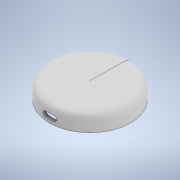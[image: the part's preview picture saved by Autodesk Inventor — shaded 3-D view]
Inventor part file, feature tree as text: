
AUTODESK INVENTOR PART (.ipt)
format: ipt  version: 2021 (Build 250183000, 183)  size: 358,400 bytes
history: native  units: mm
features: plane x4, sketch x4, extrude x3, fillet x3, revolve x1
ambient origin geometry x8: Origin, YZ Plane, XZ Plane, XY Plane, X Axis, Y Axis, Z Axis, Center Point
bodies: Volumenkörper1 (feature_tree)
feature tree (15):
  revolve  "Umdrehung1"
  extrude  "Extrusion1"  Depth=2.0mm
  plane  "Arbeitsebene2"
  sketch  "Skizze3"  dims[d9=90.0deg d11=1.78mm d12=0.0mm d13=27.4mm d14=9.0mm]
  plane  "Arbeitsebene3"
  extrude  "Extrusion2"  Depth=11.0mm
  fillet  "Rundung1"  Radius=9.0mm
  extrude  "Extrusion3"  Depth=1.78mm TaperAngle=0.0deg
  fillet  "Rundung2"  Radius=27.4mm
  fillet  "Rundung5"  Radius=9.0mm
  plane  "Arbeitsebene8"
  sketch  "Skizze1"  dims[d0=25.3mm d2=2.0mm]
  sketch  "Skizze2"  dims[d4=26.7mm d6=11.0mm d7=9.0mm]
  sketch  "Skizze4"  dims[d15=3.25mm d16=4.5mm d18=1.625mm d19=-27.4mm d21=0.0mm d22=7.61mm d23=5.1mm d24=5.1mm d25=5.1mm d26=9.0mm d27=0.0mm d28=9.0mm d29=0.0mm d30=5.0mm d31=0.0mm d32=0.3mm d33=5.0mm d34=0.0mm d35=0.3mm d49=25.3mm d50=0.3mm d53=-1.8mm d54=-1.6mm d17=0.25mm d20=0.75mm]
  plane  "Arbeitsebene7"
